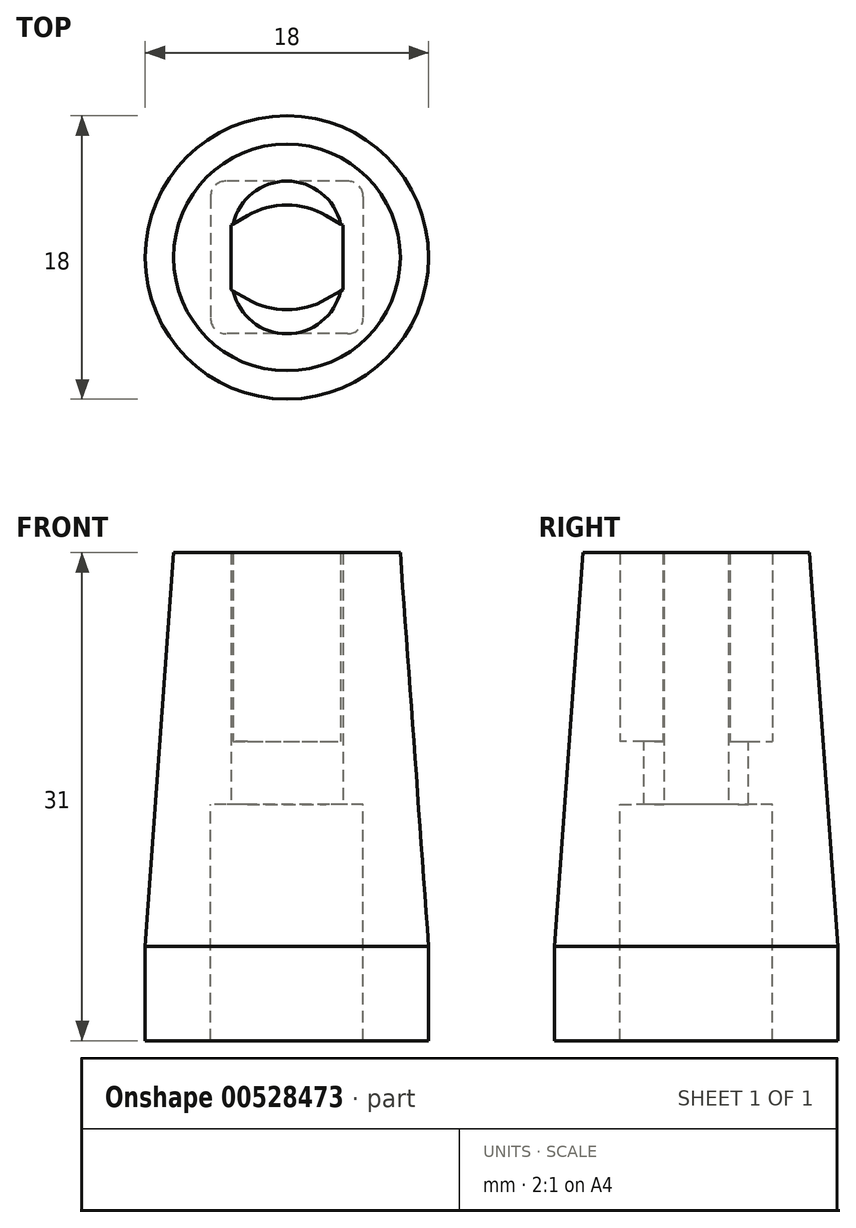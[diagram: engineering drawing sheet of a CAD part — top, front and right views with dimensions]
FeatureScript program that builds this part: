
annotation { "Feature Type Name" : "Feature", "Feature Type Description" : "" }
export const myFeature = defineFeature(function(context is Context, id is Id, definition is map)
    precondition{}
    {
        {
            var Q0;
            Q0=qCreatedBy(makeId("Top.planeOp"),FACE);
            var sketch = newSketch(context, id + "F0", { "sketchPlane" : qUnion([Q0])});
            skCircle(sketch, "E0.cCircle", {"center": v(0, 0) * mm, "radius": 3.55 * mm, "construction": true});
            skLineSegment(sketch, "E0.0", {"start": v(3.55, 2.05) * mm, "end": v(3.55, -2.05) * mm});
            skLineSegment(sketch, "E0.1", {"start": v(3.55, -2.05) * mm, "end": v(0, -4.1) * mm});
            skLineSegment(sketch, "E0.2", {"start": v(0, -4.1) * mm, "end": v(-3.55, -2.05) * mm});
            skLineSegment(sketch, "E0.3", {"start": v(-3.55, -2.05) * mm, "end": v(-3.55, 2.05) * mm});
            skLineSegment(sketch, "E0.4", {"start": v(-3.55, 2.05) * mm, "end": v(0, 4.1) * mm});
            skLineSegment(sketch, "E0.5", {"start": v(0, 4.1) * mm, "end": v(3.55, 2.05) * mm});
            skPoint(sketch, "E0.0.midPoint", {"position": v(3.55, 0) * mm});
            skLineSegment(sketch, "E1.bottom", {"start": v(3.5, 1.35) * mm, "end": v(-3.5, 1.35) * mm, "construction": true});
            skLineSegment(sketch, "E1.top", {"start": v(3.5, -1.35) * mm, "end": v(-3.5, -1.35) * mm, "construction": true});
            skLineSegment(sketch, "E1.left", {"start": v(3.5, 1.35) * mm, "end": v(3.5, -1.35) * mm});
            skLineSegment(sketch, "E1.right", {"start": v(-3.5, 1.35) * mm, "end": v(-3.5, -1.35) * mm});
            skArc(sketch, "E2", {"start": v(3.5, 1.35) * mm, "mid": v(0, 4.85) * mm, "end": v(-3.5, 1.35) * mm});
            skArc(sketch, "E3", {"start": v(-3.5, -1.35) * mm, "mid": v(0, -4.85) * mm, "end": v(3.5, -1.35) * mm});
            skCircle(sketch, "E4", {"center": v(0, 0) * mm, "radius": 9 * mm});
            skLineSegment(sketch, "E5.bottom", {"start": v(4.85, 4.85) * mm, "end": v(-4.85, 4.85) * mm});
            skLineSegment(sketch, "E5.top", {"start": v(4.85, -4.85) * mm, "end": v(-4.85, -4.85) * mm});
            skLineSegment(sketch, "E5.left", {"start": v(4.85, 4.85) * mm, "end": v(4.85, -4.85) * mm});
            skLineSegment(sketch, "E5.right", {"start": v(-4.85, 4.85) * mm, "end": v(-4.85, -4.85) * mm});
            skSolve(sketch);
        }
        {
            var Q0;
            {var subQ5=sQuery(id+"F0.wireOp",EDGE,"E0.0");Q0=makeQuery(id+"F0.imprint","IMPRINT",FACE,{"disambiguationData":[TD([[makeQuery(id+"F0.imprint","IMPRINT",EDGE,{"derivedFrom":subQ5}),1.0]])]});}
            var Q1;
            Q1=makeQuery(id+"F0.imprint","IMPRINT",FACE,{"disambiguationData":[TD([[makeQuery(id+"F0.imprint","IMPRINT",EDGE,{"derivedFrom":sQuery(id+"F0.wireOp",EDGE,"E4")}),1.0]])]});
            var Q2;
            {var subQ1=sQuery(id+"F0.wireOp",EDGE,"E0.3");Q2=makeQuery(id+"F0.imprint","IMPRINT",FACE,{"disambiguationData":[TD([[makeQuery(id+"F0.imprint","IMPRINT",EDGE,{"derivedFrom":subQ1}),1.0]])]});}
            extrude(context, id + "F1", {"entities" : qUnion([Q0, Q1, Q2]), "depth" : 16 * mm, "offsetDistance" : 25 * mm});
        }
        {
            var Q0;
            {var subQ0=sQuery(id+"F0.wireOp",EDGE,"E0.2");var subQ1=sQuery(id+"F0.wireOp",EDGE,"E0.1");var subQ2=makeQuery(id+"F0.imprint","INTERSECT",VERTEX,{"derivedFrom":[subQ1,subQ0]});Q0=makeQuery(id+"F0.imprint","IMPRINT",FACE,{"disambiguationData":[TD([[makeQuery(id+"F0.imprint","IMPRINT",EDGE,{"disambiguationData":[TD([[subQ2,1.0]])],"derivedFrom":subQ1}),1.0]])]});}
            var Q1;
            {var subQ0=sQuery(id+"F0.wireOp",EDGE,"E0.5");var subQ1=sQuery(id+"F0.wireOp",EDGE,"E0.4");var subQ2=makeQuery(id+"F0.imprint","INTERSECT",VERTEX,{"derivedFrom":[subQ1,subQ0]});Q1=makeQuery(id+"F0.imprint","IMPRINT",FACE,{"disambiguationData":[TD([[makeQuery(id+"F0.imprint","IMPRINT",EDGE,{"disambiguationData":[TD([[subQ2,1.0]])],"derivedFrom":subQ1}),1.0]])]});}
            extrude(context, id + "F2", {"entities" : qUnion([Q0, Q1]), "operationType" : NewBodyOperationType.ADD, "depth" : 4 * mm, "offsetDistance" : 25 * mm});
        }
        {
            var Q0;
            Q0=makeQuery(id+"F0.imprint","IMPRINT",FACE,{"disambiguationData":[TD([[makeQuery(id+"F0.imprint","IMPRINT",EDGE,{"derivedFrom":sQuery(id+"F0.wireOp",EDGE,"E4")}),1.0]])]});
            extrude(context, id + "F3", {"entities" : qUnion([Q0]), "operationType" : NewBodyOperationType.ADD, "oppositeDirection" : true, "depth" : 15 * mm, "offsetDistance" : 25 * mm});
        }
        {
            var Q0;
            Q0=makeQuery(id+"F2.opExtrude","SWEPT_EDGE",EDGE,{"disambiguationData":[OSD([sQuery(id+"F0.wireOp",EDGE,"E0.1"),sQuery(id+"F0.wireOp",EDGE,"E0.2")])]});
            var Q1;
            Q1=makeQuery(id+"F2.opExtrude","SWEPT_EDGE",EDGE,{"disambiguationData":[OSD([sQuery(id+"F0.wireOp",EDGE,"E0.4"),sQuery(id+"F0.wireOp",EDGE,"E0.5")])]});
            fillet(context, id + "F4", {"entities" : qUnion([Q0, Q1]), "tangentPropagation" : true, "radius" : 5 * mm, "defaultsChanged" : false, "vertexSettings" : [], "allowEdgeOverflow" : false});
        }
        {
            var Q0;
            Q0=makeQuery(id+"F3.opExtrude","SWEPT_EDGE",EDGE,{"disambiguationData":[OSD([sQuery(id+"F0.wireOp",EDGE,"E5.top"),sQuery(id+"F0.wireOp",EDGE,"E5.right")])]});
            var Q1;
            Q1=makeQuery(id+"F3.opExtrude","SWEPT_EDGE",EDGE,{"disambiguationData":[OSD([sQuery(id+"F0.wireOp",EDGE,"E5.top"),sQuery(id+"F0.wireOp",EDGE,"E5.left")])]});
            var Q2;
            Q2=makeQuery(id+"F3.opExtrude","SWEPT_EDGE",EDGE,{"disambiguationData":[OSD([sQuery(id+"F0.wireOp",EDGE,"E5.bottom"),sQuery(id+"F0.wireOp",EDGE,"E5.left")])]});
            var Q3;
            Q3=makeQuery(id+"F3.opExtrude","SWEPT_EDGE",EDGE,{"disambiguationData":[OSD([sQuery(id+"F0.wireOp",EDGE,"E5.bottom"),sQuery(id+"F0.wireOp",EDGE,"E5.right")])]});
            var Q4;
            Q4=makeQuery(id+"F3.opExtrude","CAP_EDGE",EDGE,{"disambiguationData":[OSD([sQuery(id+"F0.wireOp",EDGE,"E5.top")])],"isStart":true});
            var Q5;
            Q5=makeQuery(id+"F3.opExtrude","CAP_EDGE",EDGE,{"disambiguationData":[OSD([sQuery(id+"F0.wireOp",EDGE,"E5.right")])],"isStart":true});
            var Q6;
            Q6=makeQuery(id+"F3.opExtrude","CAP_EDGE",EDGE,{"disambiguationData":[OSD([sQuery(id+"F0.wireOp",EDGE,"E5.bottom")])],"isStart":true});
            var Q7;
            Q7=makeQuery(id+"F3.opExtrude","CAP_EDGE",EDGE,{"disambiguationData":[OSD([sQuery(id+"F0.wireOp",EDGE,"E5.left")])],"isStart":true});
            fillet(context, id + "F5", {"entities" : qUnion([Q0, Q1, Q2, Q3, Q4, Q5, Q6, Q7]), "radius" : 1 * mm, "tangentPropagation" : true, "defaultsChanged" : false, "vertexSettings" : [], "allowEdgeOverflow" : false});
        }
        {
            var Q0;
            Q0=makeQuery(id+"F1.opExtrude","CAP_EDGE",EDGE,{"disambiguationData":[OSD([sQuery(id+"F0.wireOp",EDGE,"E4")])],"isStart":false});
            chamfer(context, id + "F6", {"entities" : qUnion([Q0]), "chamferType" : ChamferType.TWO_OFFSETS, "width1" : 1.8 * mm, "oppositeDirection" : false, "width2" : 25 * mm, "tangentPropagation" : true});
        }
    });
